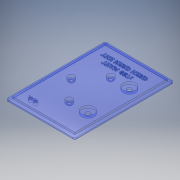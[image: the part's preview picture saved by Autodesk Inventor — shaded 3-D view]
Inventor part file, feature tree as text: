
AUTODESK INVENTOR PART (.ipt)
format: ipt  version: 2017 SP1 (Build 210196100, 196)  size: 521,216 bytes
history: native  units: in
note: dims shown in document units (in); Inventor stores cm internally (conversion verified against a paired STEP export)
features: sketch x7, extrude x4, hole x3, projected_geometry x3, chamfer x1, fillet x1
ambient origin geometry x8: Origin, YZ Plane, XZ Plane, XY Plane, X Axis, Y Axis, Z Axis, Center Point
bodies: Solid1 (feature_tree)
feature tree (19):
  extrude  "Extrusion1"  Depth=4.2in
  extrude  "Extrusion2"  Depth=0.2in
  chamfer  "Chamfer1"  Distance=0.125in
  fillet  "Fillet1"  Radius=0.125in
  hole  "Hole3"  [1 undecoded]
  hole  "Hole4"  [1 undecoded]
  extrude  "Extrusion4"  Depth=2.28in
  hole  "Hole5"  [1 undecoded]
  extrude  "Extrusion5"  Depth=1.14in
  sketch  "Sketch1"  dims[d0=6.05in d1=4.2in]
  sketch  "Sketch2"  dims[d2=0.125in d3=0.0in d4=0.2in d5=0.125in d6=0.0in]
  projected_geometry  "Projected Loop1"
  sketch  "Sketch6"  dims[d35=0.05in d36=0.125in d37=45.0deg d38=0.125in]
  projected_geometry  "Projected Loop4"
  sketch  "Sketch7"  dims[d39=1.5616in d40=1.5616in]
  sketch  "Sketch8"  dims[d41=2.5267in d42=0.76in]
  sketch  "Sketch9"  dims[d43=0.76in d44=2.28in]
  projected_geometry  "Projected Loop5"
  sketch  "Sketch10"  dims[d45=1.14in d46=1.14in d47=0.25in d48=0.75in d49=0.4in d50=0.1625in d51=0.5635in d52=1.0in d53=0.8108in d54=1.14in d55=1.14in d56=0.275in d57=0.75in d58=0.75in d59=0.15in d60=0.5635in d61=1.0in d62=0.8108in d63=0.23in d64=0.3in d65=0.75in d66=0.75in d67=0.125in d68=0.0in d69=0.0625in d70=0.0625in d71=0.0625in d72=0.0625in d73=0.125in d74=0.08in d75=0.75in d76=1.0in d77=0.15in d78=0.5635in d79=1.0in d80=0.8108in d81=1.0in d82=3.0in d83=0.15in d84=0.15in d85=0.05in d86=0.0in]
note: 3 required parameter values undecoded (feature->parameter linkage not recoverable at this tier; creation-order binding heuristic only, values carry confidence <= 0.55)
